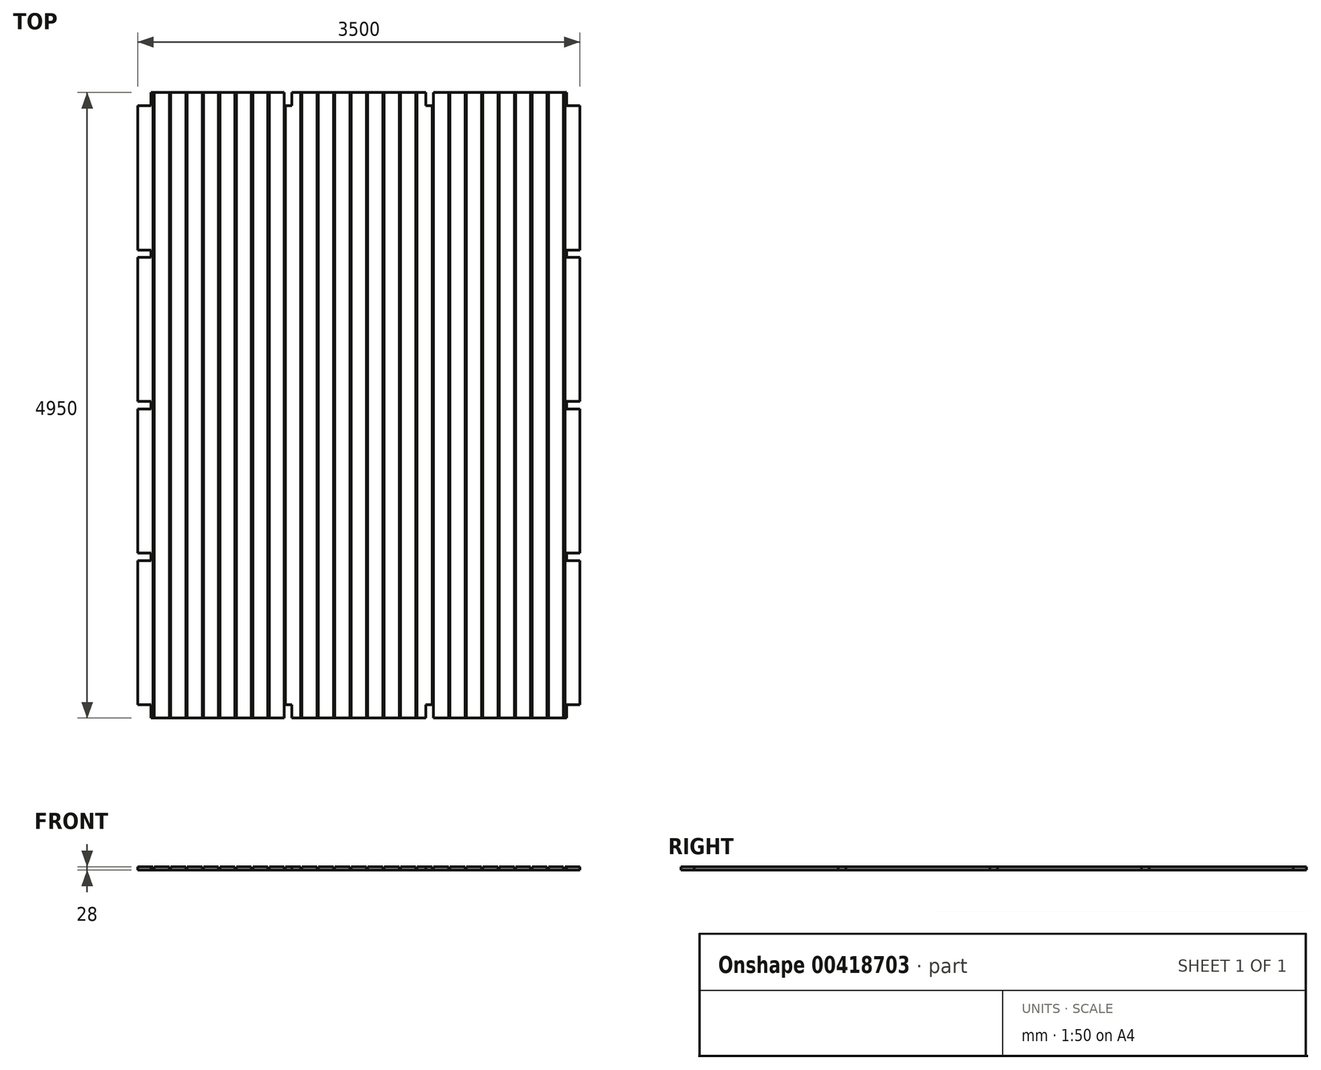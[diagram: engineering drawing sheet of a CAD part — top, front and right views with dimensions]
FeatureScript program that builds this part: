
annotation { "Feature Type Name" : "Feature", "Feature Type Description" : "" }
export const myFeature = defineFeature(function(context is Context, id is Id, definition is map)
    precondition{}
    {
        {
            var Q0;
            Q0=qCreatedBy(makeId("Front.planeOp"),FACE);
            var sketch = newSketch(context, id + "F0", { "sketchPlane" : qUnion([Q0])});
            skLineSegment(sketch, "E0.bottom", {"start": v(-1750, 0) * mm, "end": v(1750, 0) * mm});
            skLineSegment(sketch, "E0.top", {"start": v(-1750, 28) * mm, "end": v(1750, 28) * mm});
            skLineSegment(sketch, "E0.left", {"start": v(-1750, 0) * mm, "end": v(-1750, 28) * mm});
            skLineSegment(sketch, "E0.right", {"start": v(1750, 0) * mm, "end": v(1750, 28) * mm});
            skSolve(sketch);
        }
        {
            var Q0;
            Q0 = qSketchRegion(id + "F0", true);
            extrude(context, id + "F1", {"entities" : qUnion([Q0]), "endBound" : BoundingType.SYMMETRIC, "depth" : 4950 * mm, "offsetDistance" : 25 * mm});
        }
        {
            var Q0;
            Q0=qCreatedBy(makeId("Front.planeOp"),FACE);
            var sketch = newSketch(context, id + "F2", { "sketchPlane" : qUnion([Q0])});
            skLineSegment(sketch, "E1.bottom", {"start": v(-1630, 28) * mm, "end": v(-1620, 28) * mm});
            skLineSegment(sketch, "E1.top", {"start": v(-1630, 5) * mm, "end": v(-1620, 5) * mm});
            skLineSegment(sketch, "E1.left", {"start": v(-1630, 28) * mm, "end": v(-1630, 5) * mm});
            skLineSegment(sketch, "E1.right", {"start": v(-1620, 28) * mm, "end": v(-1620, 5) * mm});
            skLineSegment(sketch, "E2.1.0.0", {"start": v(-1500, 28) * mm, "end": v(-1500, 5) * mm});
            skLineSegment(sketch, "E2.1.0.1", {"start": v(-1490, 28) * mm, "end": v(-1490, 5) * mm});
            skLineSegment(sketch, "E2.1.0.2", {"start": v(-1500, 5) * mm, "end": v(-1490, 5) * mm});
            skLineSegment(sketch, "E2.1.0.3", {"start": v(-1500, 28) * mm, "end": v(-1490, 28) * mm});
            skLineSegment(sketch, "E2.2.0.0", {"start": v(-1370, 28) * mm, "end": v(-1370, 5) * mm});
            skLineSegment(sketch, "E2.2.0.1", {"start": v(-1360, 28) * mm, "end": v(-1360, 5) * mm});
            skLineSegment(sketch, "E2.2.0.2", {"start": v(-1370, 5) * mm, "end": v(-1360, 5) * mm});
            skLineSegment(sketch, "E2.2.0.3", {"start": v(-1370, 28) * mm, "end": v(-1360, 28) * mm});
            skLineSegment(sketch, "E2.3.0.0", {"start": v(-1240, 28) * mm, "end": v(-1240, 5) * mm});
            skLineSegment(sketch, "E2.3.0.1", {"start": v(-1230, 28) * mm, "end": v(-1230, 5) * mm});
            skLineSegment(sketch, "E2.3.0.2", {"start": v(-1240, 5) * mm, "end": v(-1230, 5) * mm});
            skLineSegment(sketch, "E2.3.0.3", {"start": v(-1240, 28) * mm, "end": v(-1230, 28) * mm});
            skLineSegment(sketch, "E2.4.0.0", {"start": v(-1110, 28) * mm, "end": v(-1110, 5) * mm});
            skLineSegment(sketch, "E2.4.0.1", {"start": v(-1100, 28) * mm, "end": v(-1100, 5) * mm});
            skLineSegment(sketch, "E2.4.0.2", {"start": v(-1110, 5) * mm, "end": v(-1100, 5) * mm});
            skLineSegment(sketch, "E2.4.0.3", {"start": v(-1110, 28) * mm, "end": v(-1100, 28) * mm});
            skLineSegment(sketch, "E2.5.0.0", {"start": v(-980, 28) * mm, "end": v(-980, 5) * mm});
            skLineSegment(sketch, "E2.5.0.1", {"start": v(-970, 28) * mm, "end": v(-970, 5) * mm});
            skLineSegment(sketch, "E2.5.0.2", {"start": v(-980, 5) * mm, "end": v(-970, 5) * mm});
            skLineSegment(sketch, "E2.5.0.3", {"start": v(-980, 28) * mm, "end": v(-970, 28) * mm});
            skLineSegment(sketch, "E2.6.0.0", {"start": v(-850, 28) * mm, "end": v(-850, 5) * mm});
            skLineSegment(sketch, "E2.6.0.1", {"start": v(-840, 28) * mm, "end": v(-840, 5) * mm});
            skLineSegment(sketch, "E2.6.0.2", {"start": v(-850, 5) * mm, "end": v(-840, 5) * mm});
            skLineSegment(sketch, "E2.6.0.3", {"start": v(-850, 28) * mm, "end": v(-840, 28) * mm});
            skLineSegment(sketch, "E2.7.0.0", {"start": v(-720, 28) * mm, "end": v(-720, 5) * mm});
            skLineSegment(sketch, "E2.7.0.1", {"start": v(-710, 28) * mm, "end": v(-710, 5) * mm});
            skLineSegment(sketch, "E2.7.0.2", {"start": v(-720, 5) * mm, "end": v(-710, 5) * mm});
            skLineSegment(sketch, "E2.7.0.3", {"start": v(-720, 28) * mm, "end": v(-710, 28) * mm});
            skLineSegment(sketch, "E2.8.0.0", {"start": v(-590, 28) * mm, "end": v(-590, 5) * mm});
            skLineSegment(sketch, "E2.8.0.1", {"start": v(-580, 28) * mm, "end": v(-580, 5) * mm});
            skLineSegment(sketch, "E2.8.0.2", {"start": v(-590, 5) * mm, "end": v(-580, 5) * mm});
            skLineSegment(sketch, "E2.8.0.3", {"start": v(-590, 28) * mm, "end": v(-580, 28) * mm});
            skLineSegment(sketch, "E2.9.0.0", {"start": v(-460, 28) * mm, "end": v(-460, 5) * mm});
            skLineSegment(sketch, "E2.9.0.1", {"start": v(-450, 28) * mm, "end": v(-450, 5) * mm});
            skLineSegment(sketch, "E2.9.0.2", {"start": v(-460, 5) * mm, "end": v(-450, 5) * mm});
            skLineSegment(sketch, "E2.9.0.3", {"start": v(-460, 28) * mm, "end": v(-450, 28) * mm});
            skLineSegment(sketch, "E2.10.0.0", {"start": v(-330, 28) * mm, "end": v(-330, 5) * mm});
            skLineSegment(sketch, "E2.10.0.1", {"start": v(-320, 28) * mm, "end": v(-320, 5) * mm});
            skLineSegment(sketch, "E2.10.0.2", {"start": v(-330, 5) * mm, "end": v(-320, 5) * mm});
            skLineSegment(sketch, "E2.10.0.3", {"start": v(-330, 28) * mm, "end": v(-320, 28) * mm});
            skLineSegment(sketch, "E2.11.0.0", {"start": v(-200, 28) * mm, "end": v(-200, 5) * mm});
            skLineSegment(sketch, "E2.11.0.1", {"start": v(-190, 28) * mm, "end": v(-190, 5) * mm});
            skLineSegment(sketch, "E2.11.0.2", {"start": v(-200, 5) * mm, "end": v(-190, 5) * mm});
            skLineSegment(sketch, "E2.11.0.3", {"start": v(-200, 28) * mm, "end": v(-190, 28) * mm});
            skLineSegment(sketch, "E2.12.0.0", {"start": v(-70, 28) * mm, "end": v(-70, 5) * mm});
            skLineSegment(sketch, "E2.12.0.1", {"start": v(-60, 28) * mm, "end": v(-60, 5) * mm});
            skLineSegment(sketch, "E2.12.0.2", {"start": v(-70, 5) * mm, "end": v(-60, 5) * mm});
            skLineSegment(sketch, "E2.12.0.3", {"start": v(-70, 28) * mm, "end": v(-60, 28) * mm});
            skLineSegment(sketch, "E2.13.0.0", {"start": v(60, 28) * mm, "end": v(60, 5) * mm});
            skLineSegment(sketch, "E2.13.0.1", {"start": v(70, 28) * mm, "end": v(70, 5) * mm});
            skLineSegment(sketch, "E2.13.0.2", {"start": v(60, 5) * mm, "end": v(70, 5) * mm});
            skLineSegment(sketch, "E2.13.0.3", {"start": v(60, 28) * mm, "end": v(70, 28) * mm});
            skLineSegment(sketch, "E2.14.0.0", {"start": v(190, 28) * mm, "end": v(190, 5) * mm});
            skLineSegment(sketch, "E2.14.0.1", {"start": v(200, 28) * mm, "end": v(200, 5) * mm});
            skLineSegment(sketch, "E2.14.0.2", {"start": v(190, 5) * mm, "end": v(200, 5) * mm});
            skLineSegment(sketch, "E2.14.0.3", {"start": v(190, 28) * mm, "end": v(200, 28) * mm});
            skLineSegment(sketch, "E2.15.0.0", {"start": v(320, 28) * mm, "end": v(320, 5) * mm});
            skLineSegment(sketch, "E2.15.0.1", {"start": v(330, 28) * mm, "end": v(330, 5) * mm});
            skLineSegment(sketch, "E2.15.0.2", {"start": v(320, 5) * mm, "end": v(330, 5) * mm});
            skLineSegment(sketch, "E2.15.0.3", {"start": v(320, 28) * mm, "end": v(330, 28) * mm});
            skLineSegment(sketch, "E2.16.0.0", {"start": v(450, 28) * mm, "end": v(450, 5) * mm});
            skLineSegment(sketch, "E2.16.0.1", {"start": v(460, 28) * mm, "end": v(460, 5) * mm});
            skLineSegment(sketch, "E2.16.0.2", {"start": v(450, 5) * mm, "end": v(460, 5) * mm});
            skLineSegment(sketch, "E2.16.0.3", {"start": v(450, 28) * mm, "end": v(460, 28) * mm});
            skLineSegment(sketch, "E2.17.0.0", {"start": v(580, 28) * mm, "end": v(580, 5) * mm});
            skLineSegment(sketch, "E2.17.0.1", {"start": v(590, 28) * mm, "end": v(590, 5) * mm});
            skLineSegment(sketch, "E2.17.0.2", {"start": v(580, 5) * mm, "end": v(590, 5) * mm});
            skLineSegment(sketch, "E2.17.0.3", {"start": v(580, 28) * mm, "end": v(590, 28) * mm});
            skLineSegment(sketch, "E2.18.0.0", {"start": v(710, 28) * mm, "end": v(710, 5) * mm});
            skLineSegment(sketch, "E2.18.0.1", {"start": v(720, 28) * mm, "end": v(720, 5) * mm});
            skLineSegment(sketch, "E2.18.0.2", {"start": v(710, 5) * mm, "end": v(720, 5) * mm});
            skLineSegment(sketch, "E2.18.0.3", {"start": v(710, 28) * mm, "end": v(720, 28) * mm});
            skLineSegment(sketch, "E2.19.0.0", {"start": v(840, 28) * mm, "end": v(840, 5) * mm});
            skLineSegment(sketch, "E2.19.0.1", {"start": v(850, 28) * mm, "end": v(850, 5) * mm});
            skLineSegment(sketch, "E2.19.0.2", {"start": v(840, 5) * mm, "end": v(850, 5) * mm});
            skLineSegment(sketch, "E2.19.0.3", {"start": v(840, 28) * mm, "end": v(850, 28) * mm});
            skLineSegment(sketch, "E2.20.0.0", {"start": v(970, 28) * mm, "end": v(970, 5) * mm});
            skLineSegment(sketch, "E2.20.0.1", {"start": v(980, 28) * mm, "end": v(980, 5) * mm});
            skLineSegment(sketch, "E2.20.0.2", {"start": v(970, 5) * mm, "end": v(980, 5) * mm});
            skLineSegment(sketch, "E2.20.0.3", {"start": v(970, 28) * mm, "end": v(980, 28) * mm});
            skLineSegment(sketch, "E2.21.0.0", {"start": v(1100, 28) * mm, "end": v(1100, 5) * mm});
            skLineSegment(sketch, "E2.21.0.1", {"start": v(1110, 28) * mm, "end": v(1110, 5) * mm});
            skLineSegment(sketch, "E2.21.0.2", {"start": v(1100, 5) * mm, "end": v(1110, 5) * mm});
            skLineSegment(sketch, "E2.21.0.3", {"start": v(1100, 28) * mm, "end": v(1110, 28) * mm});
            skLineSegment(sketch, "E2.direction1", {"start": v(-1630, 5) * mm, "end": v(-1500, 5) * mm, "construction": true});
            skLineSegment(sketch, "E3.0.22.0", {"start": v(1230, 28) * mm, "end": v(1230, 5) * mm});
            skLineSegment(sketch, "E3.3.22.0", {"start": v(1240, 28) * mm, "end": v(1240, 5) * mm});
            skLineSegment(sketch, "E3.6.22.0", {"start": v(1230, 5) * mm, "end": v(1240, 5) * mm});
            skLineSegment(sketch, "E3.9.22.0", {"start": v(1230, 28) * mm, "end": v(1240, 28) * mm});
            skLineSegment(sketch, "E3.0.23.0", {"start": v(1360, 28) * mm, "end": v(1360, 5) * mm});
            skLineSegment(sketch, "E3.3.23.0", {"start": v(1370, 28) * mm, "end": v(1370, 5) * mm});
            skLineSegment(sketch, "E3.6.23.0", {"start": v(1360, 5) * mm, "end": v(1370, 5) * mm});
            skLineSegment(sketch, "E3.9.23.0", {"start": v(1360, 28) * mm, "end": v(1370, 28) * mm});
            skLineSegment(sketch, "E4.0.24.0", {"start": v(1490, 28) * mm, "end": v(1490, 5) * mm});
            skLineSegment(sketch, "E4.3.24.0", {"start": v(1500, 28) * mm, "end": v(1500, 5) * mm});
            skLineSegment(sketch, "E4.6.24.0", {"start": v(1490, 5) * mm, "end": v(1500, 5) * mm});
            skLineSegment(sketch, "E4.9.24.0", {"start": v(1490, 28) * mm, "end": v(1500, 28) * mm});
            skLineSegment(sketch, "E5.0.25.0", {"start": v(1620, 28) * mm, "end": v(1620, 5) * mm});
            skLineSegment(sketch, "E5.3.25.0", {"start": v(1630, 28) * mm, "end": v(1630, 5) * mm});
            skLineSegment(sketch, "E5.6.25.0", {"start": v(1620, 5) * mm, "end": v(1630, 5) * mm});
            skLineSegment(sketch, "E5.9.25.0", {"start": v(1620, 28) * mm, "end": v(1630, 28) * mm});
            skSolve(sketch);
        }
        {
            var Q0;
            Q0 = qSketchRegion(id + "F2", true);
            extrude(context, id + "F3", {"entities" : qUnion([Q0]), "operationType" : NewBodyOperationType.REMOVE, "endBound" : BoundingType.UP_TO_NEXT, "oppositeDirection" : true, "depth" : 25 * mm, "offsetDistance" : 25 * mm, "hasSecondDirection" : true, "secondDirectionBound" : SecondDirectionBoundingType.UP_TO_NEXT, "secondDirectionOppositeDirection" : false, "secondDirectionDepth" : 25 * mm});
        }
        {
            var Q0;
            Q0=qCreatedBy(makeId("Top.planeOp"),FACE);
            var sketch = newSketch(context, id + "F4", { "sketchPlane" : qUnion([Q0])});
            skLineSegment(sketch, "E6.bottom", {"start": v(-1750, -2475) * mm, "end": v(-1645, -2475) * mm});
            skLineSegment(sketch, "E6.top", {"start": v(-1750, -2370) * mm, "end": v(-1645, -2370) * mm});
            skLineSegment(sketch, "E6.left", {"start": v(-1750, -2475) * mm, "end": v(-1750, -2370) * mm});
            skLineSegment(sketch, "E6.right", {"start": v(-1645, -2475) * mm, "end": v(-1645, -2370) * mm});
            skLineSegment(sketch, "E7.bottom", {"start": v(1750, -2475) * mm, "end": v(1645, -2475) * mm});
            skLineSegment(sketch, "E7.top", {"start": v(1750, -2370) * mm, "end": v(1645, -2370) * mm});
            skLineSegment(sketch, "E7.left", {"start": v(1750, -2475) * mm, "end": v(1750, -2370) * mm});
            skLineSegment(sketch, "E7.right", {"start": v(1645, -2475) * mm, "end": v(1645, -2370) * mm});
            skLineSegment(sketch, "E8.bottom", {"start": v(1750, 2475) * mm, "end": v(1645, 2475) * mm});
            skLineSegment(sketch, "E8.top", {"start": v(1750, 2370) * mm, "end": v(1645, 2370) * mm});
            skLineSegment(sketch, "E8.left", {"start": v(1750, 2475) * mm, "end": v(1750, 2370) * mm});
            skLineSegment(sketch, "E8.right", {"start": v(1645, 2475) * mm, "end": v(1645, 2370) * mm});
            skLineSegment(sketch, "E9.bottom", {"start": v(-1750, 2475) * mm, "end": v(-1645, 2475) * mm});
            skLineSegment(sketch, "E9.top", {"start": v(-1750, 2370) * mm, "end": v(-1645, 2370) * mm});
            skLineSegment(sketch, "E9.left", {"start": v(-1750, 2475) * mm, "end": v(-1750, 2370) * mm});
            skLineSegment(sketch, "E9.right", {"start": v(-1645, 2475) * mm, "end": v(-1645, 2370) * mm});
            skLineSegment(sketch, "E10.bottom", {"start": v(-590, -2475) * mm, "end": v(-530, -2475) * mm});
            skLineSegment(sketch, "E10.top", {"start": v(-590, -2370) * mm, "end": v(-530, -2370) * mm});
            skLineSegment(sketch, "E10.left", {"start": v(-590, -2475) * mm, "end": v(-590, -2370) * mm});
            skLineSegment(sketch, "E10.right", {"start": v(-530, -2475) * mm, "end": v(-530, -2370) * mm});
            skLineSegment(sketch, "E11.bottom", {"start": v(530, -2475) * mm, "end": v(590, -2475) * mm});
            skLineSegment(sketch, "E11.top", {"start": v(530, -2370) * mm, "end": v(590, -2370) * mm});
            skLineSegment(sketch, "E11.left", {"start": v(530, -2475) * mm, "end": v(530, -2370) * mm});
            skLineSegment(sketch, "E11.right", {"start": v(590, -2475) * mm, "end": v(590, -2370) * mm});
            skLineSegment(sketch, "E12.bottom", {"start": v(-590, 2475) * mm, "end": v(-530, 2475) * mm});
            skLineSegment(sketch, "E12.top", {"start": v(-590, 2370) * mm, "end": v(-530, 2370) * mm});
            skLineSegment(sketch, "E12.left", {"start": v(-590, 2475) * mm, "end": v(-590, 2370) * mm});
            skLineSegment(sketch, "E12.right", {"start": v(-530, 2475) * mm, "end": v(-530, 2370) * mm});
            skLineSegment(sketch, "E13.bottom", {"start": v(530, 2475) * mm, "end": v(590, 2475) * mm});
            skLineSegment(sketch, "E13.top", {"start": v(530, 2370) * mm, "end": v(590, 2370) * mm});
            skLineSegment(sketch, "E13.left", {"start": v(530, 2475) * mm, "end": v(530, 2370) * mm});
            skLineSegment(sketch, "E13.right", {"start": v(590, 2475) * mm, "end": v(590, 2370) * mm});
            skLineSegment(sketch, "E14.bottom", {"start": v(-1750, -1230) * mm, "end": v(-1645, -1230) * mm});
            skLineSegment(sketch, "E14.top", {"start": v(-1750, -1170) * mm, "end": v(-1645, -1170) * mm});
            skLineSegment(sketch, "E14.left", {"start": v(-1750, -1230) * mm, "end": v(-1750, -1170) * mm});
            skLineSegment(sketch, "E14.right", {"start": v(-1645, -1230) * mm, "end": v(-1645, -1170) * mm});
            skLineSegment(sketch, "E15.bottom", {"start": v(-1750, -30) * mm, "end": v(-1645, -30) * mm});
            skLineSegment(sketch, "E15.top", {"start": v(-1750, 30) * mm, "end": v(-1645, 30) * mm});
            skLineSegment(sketch, "E15.left", {"start": v(-1750, -30) * mm, "end": v(-1750, 30) * mm});
            skLineSegment(sketch, "E15.right", {"start": v(-1645, -30) * mm, "end": v(-1645, 30) * mm});
            skLineSegment(sketch, "E16.bottom", {"start": v(-1750, 1170) * mm, "end": v(-1645, 1170) * mm});
            skLineSegment(sketch, "E16.top", {"start": v(-1750, 1230) * mm, "end": v(-1645, 1230) * mm});
            skLineSegment(sketch, "E16.left", {"start": v(-1750, 1170) * mm, "end": v(-1750, 1230) * mm});
            skLineSegment(sketch, "E16.right", {"start": v(-1645, 1170) * mm, "end": v(-1645, 1230) * mm});
            skLineSegment(sketch, "E17.bottom", {"start": v(1750, 1230) * mm, "end": v(1645, 1230) * mm});
            skLineSegment(sketch, "E17.top", {"start": v(1750, 1170) * mm, "end": v(1645, 1170) * mm});
            skLineSegment(sketch, "E17.left", {"start": v(1750, 1230) * mm, "end": v(1750, 1170) * mm});
            skLineSegment(sketch, "E17.right", {"start": v(1645, 1230) * mm, "end": v(1645, 1170) * mm});
            skLineSegment(sketch, "E18.bottom", {"start": v(1750, 30) * mm, "end": v(1645, 30) * mm});
            skLineSegment(sketch, "E18.top", {"start": v(1750, -30) * mm, "end": v(1645, -30) * mm});
            skLineSegment(sketch, "E18.left", {"start": v(1750, 30) * mm, "end": v(1750, -30) * mm});
            skLineSegment(sketch, "E18.right", {"start": v(1645, 30) * mm, "end": v(1645, -30) * mm});
            skLineSegment(sketch, "E19.bottom", {"start": v(1750, -1170) * mm, "end": v(1645, -1170) * mm});
            skLineSegment(sketch, "E19.top", {"start": v(1750, -1230) * mm, "end": v(1645, -1230) * mm});
            skLineSegment(sketch, "E19.left", {"start": v(1750, -1170) * mm, "end": v(1750, -1230) * mm});
            skLineSegment(sketch, "E19.right", {"start": v(1645, -1170) * mm, "end": v(1645, -1230) * mm});
            skSolve(sketch);
        }
        {
            var Q0;
            Q0 = qSketchRegion(id + "F4", true);
            extrude(context, id + "F5", {"entities" : qUnion([Q0]), "operationType" : NewBodyOperationType.REMOVE, "endBound" : BoundingType.UP_TO_NEXT, "depth" : 25 * mm, "offsetDistance" : 25 * mm});
        }
    });
